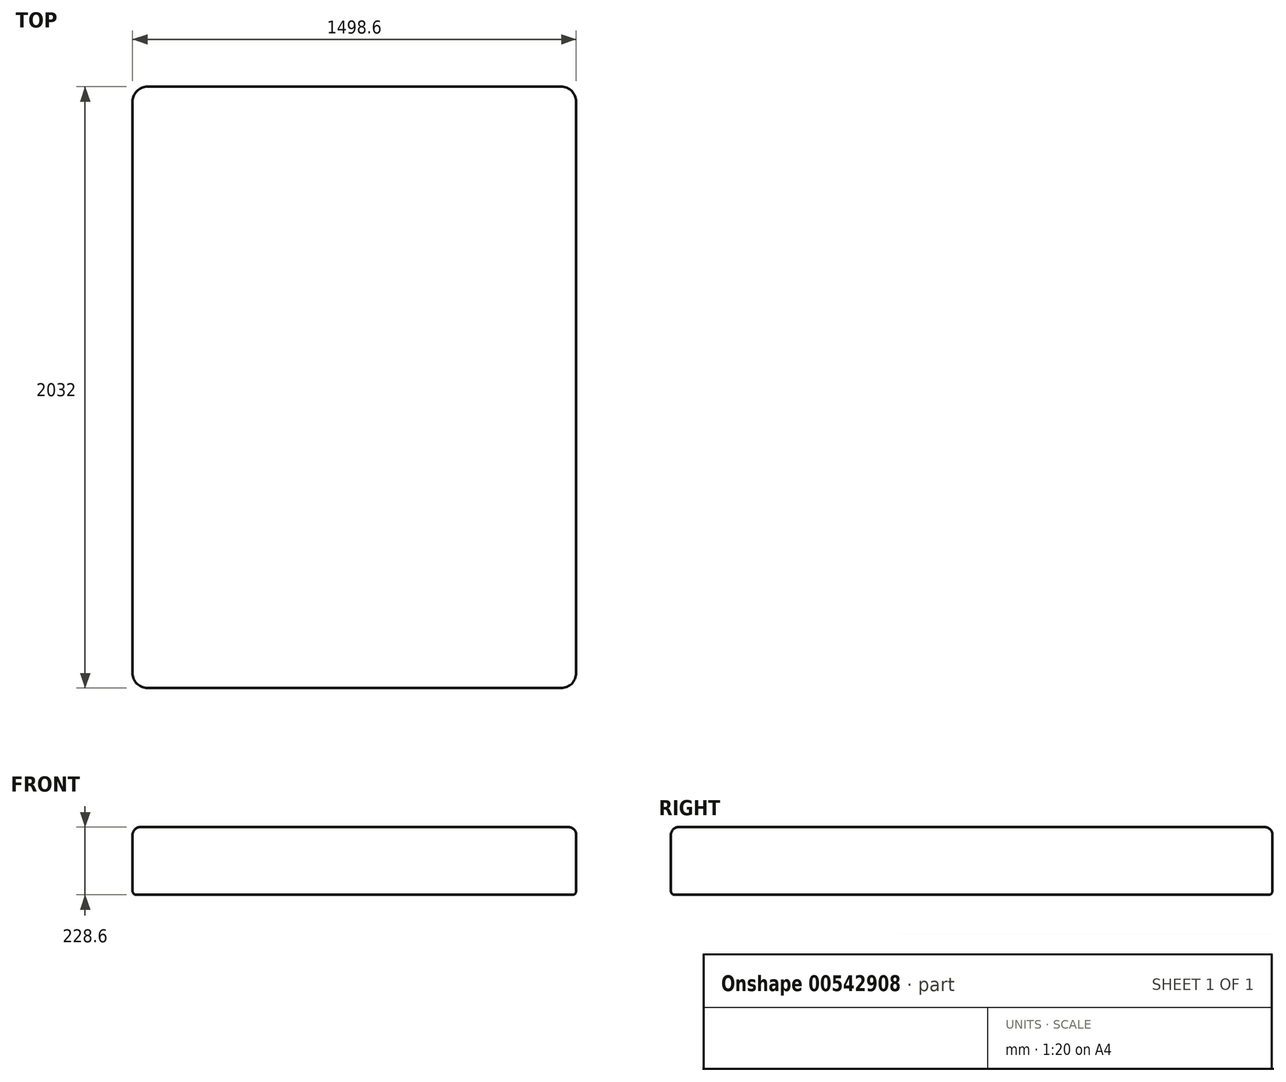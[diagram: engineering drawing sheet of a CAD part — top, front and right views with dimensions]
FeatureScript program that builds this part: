
annotation { "Feature Type Name" : "Feature", "Feature Type Description" : "" }
export const myFeature = defineFeature(function(context is Context, id is Id, definition is map)
    precondition{}
    {
        {
            var Q0;
            Q0=qCreatedBy(makeId("Top.planeOp"),FACE);
            var sketch = newSketch(context, id + "F0", { "sketchPlane" : qUnion([Q0])});
            skLineSegment(sketch, "E0.bottom", {"start": v(749.3, 1016) * mm, "end": v(-749.3, 1016) * mm});
            skLineSegment(sketch, "E0.top", {"start": v(749.3, -1016) * mm, "end": v(-749.3, -1016) * mm});
            skLineSegment(sketch, "E0.left", {"start": v(749.3, 1016) * mm, "end": v(749.3, -1016) * mm});
            skLineSegment(sketch, "E0.right", {"start": v(-749.3, 1016) * mm, "end": v(-749.3, -1016) * mm});
            skPoint(sketch, "E0.middle", {"position": v(0, 0) * mm});
            skSolve(sketch);
        }
        {
            var Q0;
            Q0=qSketchRegion(id+"F0",true);
            extrude(context, id + "F1", {"entities" : qUnion([Q0]), "depth" : 228.6 * mm});
        }
        {
            var Q0;
            Q0=makeQuery(id+"F1.opExtrude","CAP_EDGE",EDGE,{"disambiguationData":[OSD([sQuery(id+"F0.wireOp",EDGE,"E0.right")])],"isStart":false});
            var Q1;
            Q1=makeQuery(id+"F1.opExtrude","CAP_EDGE",EDGE,{"disambiguationData":[OSD([sQuery(id+"F0.wireOp",EDGE,"E0.top")])],"isStart":false});
            var Q2;
            Q2=makeQuery(id+"F1.opExtrude","CAP_EDGE",EDGE,{"disambiguationData":[OSD([sQuery(id+"F0.wireOp",EDGE,"E0.left")])],"isStart":false});
            var Q3;
            Q3=makeQuery(id+"F1.opExtrude","CAP_EDGE",EDGE,{"disambiguationData":[OSD([sQuery(id+"F0.wireOp",EDGE,"E0.bottom")])],"isStart":false});
            fillet(context, id + "F2", {"entities" : qUnion([Q0, Q1, Q2, Q3]), "radius" : 25.4 * mm, "tangentPropagation" : true, "allowEdgeOverflow" : false});
        }
        {
            var Q0;
            Q0=makeQuery(id+"F1.opExtrude","SWEPT_EDGE",EDGE,{"disambiguationData":[OSD([sQuery(id+"F0.wireOp",EDGE,"E0.top"),sQuery(id+"F0.wireOp",EDGE,"E0.right")])]});
            var Q1;
            Q1=makeQuery(id+"F1.opExtrude","SWEPT_EDGE",EDGE,{"disambiguationData":[OSD([sQuery(id+"F0.wireOp",EDGE,"E0.top"),sQuery(id+"F0.wireOp",EDGE,"E0.left")])]});
            var Q2;
            Q2=makeQuery(id+"F1.opExtrude","SWEPT_EDGE",EDGE,{"disambiguationData":[OSD([sQuery(id+"F0.wireOp",EDGE,"E0.bottom"),sQuery(id+"F0.wireOp",EDGE,"E0.right")])]});
            var Q3;
            Q3=makeQuery(id+"F1.opExtrude","SWEPT_EDGE",EDGE,{"disambiguationData":[OSD([sQuery(id+"F0.wireOp",EDGE,"E0.bottom"),sQuery(id+"F0.wireOp",EDGE,"E0.left")])]});
            fillet(context, id + "F3", {"entities" : qUnion([Q0, Q1, Q2, Q3]), "radius" : 50.8 * mm, "tangentPropagation" : true, "allowEdgeOverflow" : false});
        }
        {
            var Q0;
            Q0=makeQuery(id+"F1.opExtrude","CAP_EDGE",EDGE,{"disambiguationData":[OSD([sQuery(id+"F0.wireOp",EDGE,"E0.bottom")])],"isStart":true});
            var Q1;
            Q1=makeQuery(id+"F1.opExtrude","CAP_EDGE",EDGE,{"disambiguationData":[OSD([sQuery(id+"F0.wireOp",EDGE,"E0.right")])],"isStart":true});
            var Q2;
            Q2=makeQuery(id+"F1.opExtrude","CAP_EDGE",EDGE,{"disambiguationData":[OSD([sQuery(id+"F0.wireOp",EDGE,"E0.top")])],"isStart":true});
            fillet(context, id + "F4", {"entities" : qUnion([Q0, Q1, Q2]), "radius" : 12.7 * mm, "tangentPropagation" : true, "allowEdgeOverflow" : false});
        }
    });
